# Revit family: Faucet-Valves_and_Controls-KOHLER-K-28139T_1
name_source: partatom
category: Plumbing Fixtures
revit_build: Autodesk Revit 2017 (Build: 20160225_1515(x64)
units: mm (PartAtom-declared; Revit-internal decimal feet)

## family parameters
Cut with Voids When Loaded = No
Host = Face
OmniClass Number = 23.27.31.00
OmniClass Title = Valves
Part Type = Normal
Room Calculation Point = No
Round Connector Dimension = Use Diameter
Shared = No

## types (2) — shared parameters
ADA Compliant = No
Assembly Code = D2020
CW Connection = Yes
Cold Water Inlet = Cold Water Inlet
Date Modified = 05/26/2020
Default Elevation = 36"
Drain Included = No
Finish = Kohler-Metal-Brass
Flow Rate = 0 GPM
HW Connection = Yes
Height = 2 1/16"
Hot Water Inlet = Hot Water Inlet
Length = 3 1/16"
Manufacturer = KOHLER Co.
MasterFormat 1995 = 154300
MasterFormat 2004 = 22.41.39
Material = Brass Construction
Pressure = 116.03 psi
URL = http://www.kohler.com.cn
Vent Connection = No
Waste Connection = No
Waste Water Outlet = Waste Water Outlet
WaterSense Certified = No
Width = 11"

## per-type parameters (varying)
| type | Description | Model | Product Documentation Link | Product Page URL | Type |
| NA-Brass | Double-handle wall lavatory faucet spool stem handle spool | K-28139T-NA | http://files.kohler.com.cn | http://www.kohler.com.cn | 1 |
| DR, NA-Brass | W/M DUAL HANDLE LAV FCT VALVE | K-28139T-DR-NA |  |  | 2 |

## geometry (parser evidence)
native form markers: Sweep x4
no freeform markers — native parametric forms only
